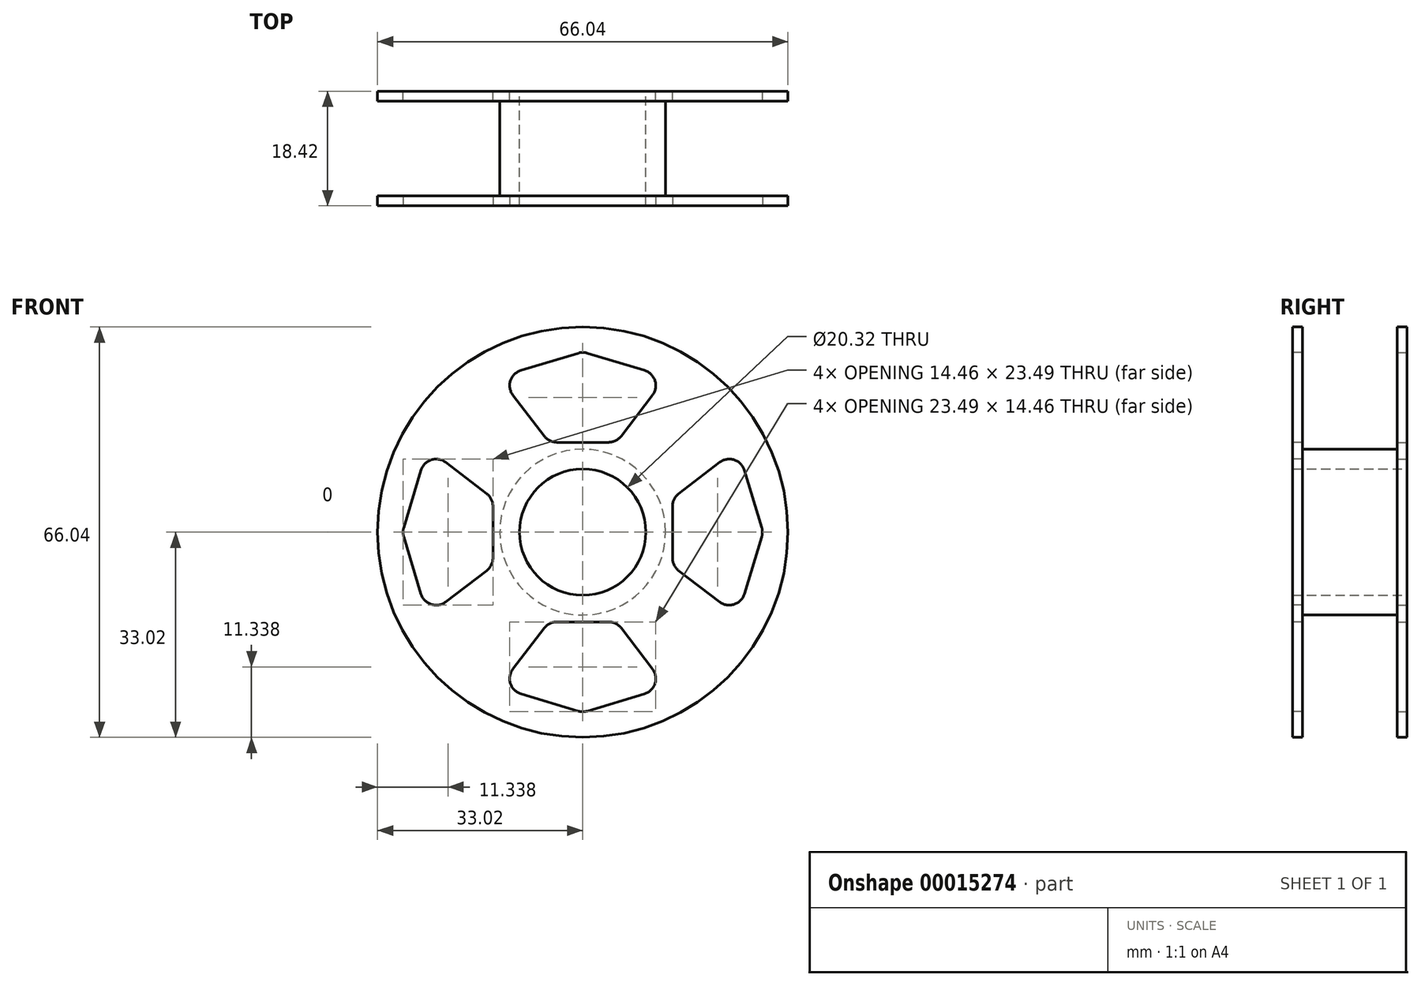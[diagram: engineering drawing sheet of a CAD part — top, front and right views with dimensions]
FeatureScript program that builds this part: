
annotation { "Feature Type Name" : "Feature", "Feature Type Description" : "" }
export const myFeature = defineFeature(function(context is Context, id is Id, definition is map)
    precondition{}
    {
        {
            var Q0;
            Q0=qCreatedBy(makeId("Front.planeOp"),FACE);
            var sketch = newSketch(context, id + "F0", { "sketchPlane" : qUnion([Q0])});
            skCircle(sketch, "E0", {"center": v(0, 0) * mm, "radius": 33.02 * mm});
            skCircle(sketch, "E1", {"center": v(0, 0) * mm, "radius": 10.16 * mm});
            skLineSegment(sketch, "E2", {"start": v(0, 14.45) * mm, "end": v(-4.17, 14.45) * mm});
            skLineSegment(sketch, "E3", {"start": v(-6.19, 15.45) * mm, "end": v(-11.23, 22.05) * mm});
            skLineSegment(sketch, "E4", {"start": v(-9.95, 26.02) * mm, "end": v(-0.73, 28.8) * mm});
            skLineSegment(sketch, "E5", {"start": v(0, 0) * mm, "end": v(0, 34.98) * mm, "construction": true});
            skLineSegment(sketch, "E6.MirrorCS", {"start": v(9.95, 26.02) * mm, "end": v(0.73, 28.8) * mm});
            skLineSegment(sketch, "E7.MirrorCS", {"start": v(6.19, 15.45) * mm, "end": v(11.23, 22.05) * mm});
            skLineSegment(sketch, "E8.MirrorCS", {"start": v(0, 14.45) * mm, "end": v(4.17, 14.45) * mm});
            skPoint(sketch, "E9.visualSharp", {"position": v(-13.46, 24.96) * mm});
            skArc(sketch, "E9.filletArc", {"start": v(-9.95, 26.02) * mm, "mid": v(-11.63, 24.37) * mm, "end": v(-11.23, 22.05) * mm});
            skPoint(sketch, "E10.visualSharp", {"position": v(-5.43, 14.45) * mm});
            skArc(sketch, "E10.filletArc", {"start": v(-6.19, 15.45) * mm, "mid": v(-5.3, 14.71) * mm, "end": v(-4.17, 14.45) * mm});
            skPoint(sketch, "E11.visualSharp", {"position": v(5.43, 14.45) * mm});
            skArc(sketch, "E11.filletArc", {"start": v(4.17, 14.45) * mm, "mid": v(5.3, 14.71) * mm, "end": v(6.19, 15.45) * mm});
            skPoint(sketch, "E12.visualSharp", {"position": v(13.46, 24.96) * mm});
            skArc(sketch, "E12.filletArc", {"start": v(11.23, 22.05) * mm, "mid": v(11.63, 24.37) * mm, "end": v(9.95, 26.02) * mm});
            skPoint(sketch, "E13.visualSharp", {"position": v(0, 29.03) * mm});
            skArc(sketch, "E13.filletArc", {"start": v(0.73, 28.8) * mm, "mid": v(0, 28.91) * mm, "end": v(-0.73, 28.8) * mm});
            skLineSegment(sketch, "E14.1.0", {"start": v(-14.45, 0) * mm, "end": v(-14.45, -4.17) * mm});
            skArc(sketch, "E14.1.1", {"start": v(-26.02, -9.95) * mm, "mid": v(-24.37, -11.63) * mm, "end": v(-22.05, -11.23) * mm});
            skLineSegment(sketch, "E14.1.2", {"start": v(-15.45, -6.19) * mm, "end": v(-22.05, -11.23) * mm});
            skPoint(sketch, "E14.1.3", {"position": v(-24.96, -13.46) * mm});
            skPoint(sketch, "E14.1.4", {"position": v(-29.03, 0) * mm});
            skLineSegment(sketch, "E14.1.5", {"start": v(-26.02, -9.95) * mm, "end": v(-28.8, -0.73) * mm});
            skPoint(sketch, "E14.1.6", {"position": v(-14.45, -5.43) * mm});
            skPoint(sketch, "E14.1.7", {"position": v(-24.96, 13.46) * mm});
            skLineSegment(sketch, "E14.1.8", {"start": v(-26.02, 9.95) * mm, "end": v(-28.8, 0.73) * mm});
            skLineSegment(sketch, "E14.1.9", {"start": v(-14.45, 0) * mm, "end": v(-14.45, 4.17) * mm});
            skPoint(sketch, "E14.1.10", {"position": v(-14.45, 5.43) * mm});
            skLineSegment(sketch, "E14.1.11", {"start": v(-15.45, 6.19) * mm, "end": v(-22.05, 11.23) * mm});
            skArc(sketch, "E14.1.12", {"start": v(-22.05, 11.23) * mm, "mid": v(-24.37, 11.63) * mm, "end": v(-26.02, 9.95) * mm});
            skArc(sketch, "E14.1.13", {"start": v(-15.45, -6.19) * mm, "mid": v(-14.71, -5.3) * mm, "end": v(-14.45, -4.17) * mm});
            skArc(sketch, "E14.1.14", {"start": v(-28.8, 0.73) * mm, "mid": v(-28.91, 0) * mm, "end": v(-28.8, -0.73) * mm});
            skArc(sketch, "E14.1.15", {"start": v(-14.45, 4.17) * mm, "mid": v(-14.71, 5.3) * mm, "end": v(-15.45, 6.19) * mm});
            skLineSegment(sketch, "E14.2.0", {"start": v(0, -14.45) * mm, "end": v(4.17, -14.45) * mm});
            skArc(sketch, "E14.2.1", {"start": v(9.95, -26.02) * mm, "mid": v(11.63, -24.37) * mm, "end": v(11.23, -22.05) * mm});
            skLineSegment(sketch, "E14.2.2", {"start": v(6.19, -15.45) * mm, "end": v(11.23, -22.05) * mm});
            skPoint(sketch, "E14.2.3", {"position": v(13.46, -24.96) * mm});
            skPoint(sketch, "E14.2.4", {"position": v(0, -29.03) * mm});
            skLineSegment(sketch, "E14.2.5", {"start": v(9.95, -26.02) * mm, "end": v(0.73, -28.8) * mm});
            skPoint(sketch, "E14.2.6", {"position": v(5.43, -14.45) * mm});
            skPoint(sketch, "E14.2.7", {"position": v(-13.46, -24.96) * mm});
            skLineSegment(sketch, "E14.2.8", {"start": v(-9.95, -26.02) * mm, "end": v(-0.73, -28.8) * mm});
            skLineSegment(sketch, "E14.2.9", {"start": v(0, -14.45) * mm, "end": v(-4.17, -14.45) * mm});
            skPoint(sketch, "E14.2.10", {"position": v(-5.43, -14.45) * mm});
            skLineSegment(sketch, "E14.2.11", {"start": v(-6.19, -15.45) * mm, "end": v(-11.23, -22.05) * mm});
            skArc(sketch, "E14.2.12", {"start": v(-11.23, -22.05) * mm, "mid": v(-11.63, -24.37) * mm, "end": v(-9.95, -26.02) * mm});
            skArc(sketch, "E14.2.13", {"start": v(6.19, -15.45) * mm, "mid": v(5.3, -14.71) * mm, "end": v(4.17, -14.45) * mm});
            skArc(sketch, "E14.2.14", {"start": v(-0.73, -28.8) * mm, "mid": v(0, -28.91) * mm, "end": v(0.73, -28.8) * mm});
            skArc(sketch, "E14.2.15", {"start": v(-4.17, -14.45) * mm, "mid": v(-5.3, -14.71) * mm, "end": v(-6.19, -15.45) * mm});
            skLineSegment(sketch, "E15.2.3.0", {"start": v(14.45, 0) * mm, "end": v(14.45, 4.17) * mm});
            skArc(sketch, "E15.3.3.0", {"start": v(26.02, 9.95) * mm, "mid": v(24.37, 11.63) * mm, "end": v(22.05, 11.23) * mm});
            skLineSegment(sketch, "E15.7.3.0", {"start": v(15.45, 6.19) * mm, "end": v(22.05, 11.23) * mm});
            skPoint(sketch, "E15.10.3.0", {"position": v(24.96, 13.46) * mm});
            skPoint(sketch, "E15.11.3.0", {"position": v(29.03, 0) * mm});
            skLineSegment(sketch, "E15.12.3.0", {"start": v(26.02, 9.95) * mm, "end": v(28.8, 0.73) * mm});
            skPoint(sketch, "E15.15.3.0", {"position": v(14.45, 5.43) * mm});
            skPoint(sketch, "E15.16.3.0", {"position": v(24.96, -13.46) * mm});
            skLineSegment(sketch, "E15.17.3.0", {"start": v(26.02, -9.95) * mm, "end": v(28.8, -0.73) * mm});
            skLineSegment(sketch, "E15.20.3.0", {"start": v(14.45, 0) * mm, "end": v(14.45, -4.17) * mm});
            skPoint(sketch, "E15.23.3.0", {"position": v(14.45, -5.43) * mm});
            skLineSegment(sketch, "E15.24.3.0", {"start": v(15.45, -6.19) * mm, "end": v(22.05, -11.23) * mm});
            skArc(sketch, "E15.27.3.0", {"start": v(22.05, -11.23) * mm, "mid": v(24.37, -11.63) * mm, "end": v(26.02, -9.95) * mm});
            skArc(sketch, "E15.31.3.0", {"start": v(15.45, 6.19) * mm, "mid": v(14.71, 5.3) * mm, "end": v(14.45, 4.17) * mm});
            skArc(sketch, "E15.35.3.0", {"start": v(28.8, -0.73) * mm, "mid": v(28.91, 0) * mm, "end": v(28.8, 0.73) * mm});
            skArc(sketch, "E15.39.3.0", {"start": v(14.45, -4.17) * mm, "mid": v(14.71, -5.3) * mm, "end": v(15.45, -6.19) * mm});
            skSolve(sketch);
        }
        {
            var Q0;
            Q0 = qSketchRegion(id + "F0", true);
            extrude(context, id + "F1", {"entities" : qUnion([Q0]), "depth" : 1.59 * mm});
        }
        {
            var Q0;
            Q0=makeQuery(id+"F1.opExtrude","CAP_FACE",FACE,{"disambiguationData":[OSD([sQuery(id+"F0.wireOp",EDGE,"E0"),sQuery(id+"F0.wireOp",EDGE,"E1"),sQuery(id+"F0.wireOp",EDGE,"E2"),sQuery(id+"F0.wireOp",EDGE,"E3"),sQuery(id+"F0.wireOp",EDGE,"E4"),sQuery(id+"F0.wireOp",EDGE,"E6.MirrorCS"),sQuery(id+"F0.wireOp",EDGE,"E7.MirrorCS"),sQuery(id+"F0.wireOp",EDGE,"E8.MirrorCS"),sQuery(id+"F0.wireOp",EDGE,"E9.filletArc"),sQuery(id+"F0.wireOp",EDGE,"E10.filletArc"),sQuery(id+"F0.wireOp",EDGE,"E11.filletArc"),sQuery(id+"F0.wireOp",EDGE,"E12.filletArc"),sQuery(id+"F0.wireOp",EDGE,"E13.filletArc"),sQuery(id+"F0.wireOp",EDGE,"E14.1.0"),sQuery(id+"F0.wireOp",EDGE,"E14.1.1"),sQuery(id+"F0.wireOp",EDGE,"E14.1.2"),sQuery(id+"F0.wireOp",EDGE,"E14.1.5"),sQuery(id+"F0.wireOp",EDGE,"E14.1.8"),sQuery(id+"F0.wireOp",EDGE,"E14.1.9"),sQuery(id+"F0.wireOp",EDGE,"E14.1.11"),sQuery(id+"F0.wireOp",EDGE,"E14.1.12"),sQuery(id+"F0.wireOp",EDGE,"E14.1.13"),sQuery(id+"F0.wireOp",EDGE,"E14.1.14"),sQuery(id+"F0.wireOp",EDGE,"E14.1.15"),sQuery(id+"F0.wireOp",EDGE,"E14.2.0"),sQuery(id+"F0.wireOp",EDGE,"E14.2.1"),sQuery(id+"F0.wireOp",EDGE,"E14.2.2"),sQuery(id+"F0.wireOp",EDGE,"E14.2.5"),sQuery(id+"F0.wireOp",EDGE,"E14.2.8"),sQuery(id+"F0.wireOp",EDGE,"E14.2.9"),sQuery(id+"F0.wireOp",EDGE,"E14.2.11"),sQuery(id+"F0.wireOp",EDGE,"E14.2.12"),sQuery(id+"F0.wireOp",EDGE,"E14.2.13"),sQuery(id+"F0.wireOp",EDGE,"E14.2.14"),sQuery(id+"F0.wireOp",EDGE,"E14.2.15")])],"isStart":false});
            var sketch = newSketch(context, id + "F2", { "sketchPlane" : qUnion([Q0])});
            skCircle(sketch, "E16.0", {"center": v(0, 0) * mm, "radius": 10.16 * mm});
            skCircle(sketch, "E17.0", {"center": v(0, 0) * mm, "radius": 13.34 * mm});
            skSolve(sketch);
        }
        {
            var Q0;
            Q0=makeQuery(id+"F2.imprint","IMPRINT",FACE,{"disambiguationData":[TD([[makeQuery(id+"F2.imprint","IMPRINT",EDGE,{"derivedFrom":sQuery(id+"F2.wireOp",EDGE,"E16.0")}),-1.0]])]});
            extrude(context, id + "F3", {"entities" : qUnion([Q0]), "operationType" : NewBodyOperationType.ADD, "depth" : 7.62 * mm});
        }
        {
            var Q0;
            Q0=makeQuery(id+"F1.opExtrude","SWEPT_BODY",BODY,{"disambiguationData":[OSD([sQuery(id+"F0.wireOp",EDGE,"E0"),sQuery(id+"F0.wireOp",EDGE,"E1"),sQuery(id+"F0.wireOp",EDGE,"E2"),sQuery(id+"F0.wireOp",EDGE,"E3"),sQuery(id+"F0.wireOp",EDGE,"E4"),sQuery(id+"F0.wireOp",EDGE,"E6.MirrorCS"),sQuery(id+"F0.wireOp",EDGE,"E7.MirrorCS"),sQuery(id+"F0.wireOp",EDGE,"E8.MirrorCS"),sQuery(id+"F0.wireOp",EDGE,"E9.filletArc"),sQuery(id+"F0.wireOp",EDGE,"E10.filletArc"),sQuery(id+"F0.wireOp",EDGE,"E11.filletArc"),sQuery(id+"F0.wireOp",EDGE,"E12.filletArc"),sQuery(id+"F0.wireOp",EDGE,"E13.filletArc"),sQuery(id+"F0.wireOp",EDGE,"E14.1.0"),sQuery(id+"F0.wireOp",EDGE,"E14.1.1"),sQuery(id+"F0.wireOp",EDGE,"E14.1.2"),sQuery(id+"F0.wireOp",EDGE,"E14.1.5"),sQuery(id+"F0.wireOp",EDGE,"E14.1.8"),sQuery(id+"F0.wireOp",EDGE,"E14.1.9"),sQuery(id+"F0.wireOp",EDGE,"E14.1.11"),sQuery(id+"F0.wireOp",EDGE,"E14.1.12"),sQuery(id+"F0.wireOp",EDGE,"E14.1.13"),sQuery(id+"F0.wireOp",EDGE,"E14.1.14"),sQuery(id+"F0.wireOp",EDGE,"E14.1.15"),sQuery(id+"F0.wireOp",EDGE,"E14.2.0"),sQuery(id+"F0.wireOp",EDGE,"E14.2.1"),sQuery(id+"F0.wireOp",EDGE,"E14.2.2"),sQuery(id+"F0.wireOp",EDGE,"E14.2.5"),sQuery(id+"F0.wireOp",EDGE,"E14.2.8"),sQuery(id+"F0.wireOp",EDGE,"E14.2.9"),sQuery(id+"F0.wireOp",EDGE,"E14.2.11"),sQuery(id+"F0.wireOp",EDGE,"E14.2.12"),sQuery(id+"F0.wireOp",EDGE,"E14.2.13"),sQuery(id+"F0.wireOp",EDGE,"E14.2.14"),sQuery(id+"F0.wireOp",EDGE,"E14.2.15")])]});
            var Q1;
            Q1=makeQuery(id+"F3.opExtrude","CAP_FACE",FACE,{"disambiguationData":[OSD([sQuery(id+"F2.wireOp",EDGE,"E16.0"),sQuery(id+"F2.wireOp",EDGE,"E17.0")])],"isStart":false});
            mirror(context, id + "F4", {"operationType" : NewBodyOperationType.ADD, "entities" : qUnion([Q0]), "mirrorPlane" : qUnion([Q1])});
        }
    });
